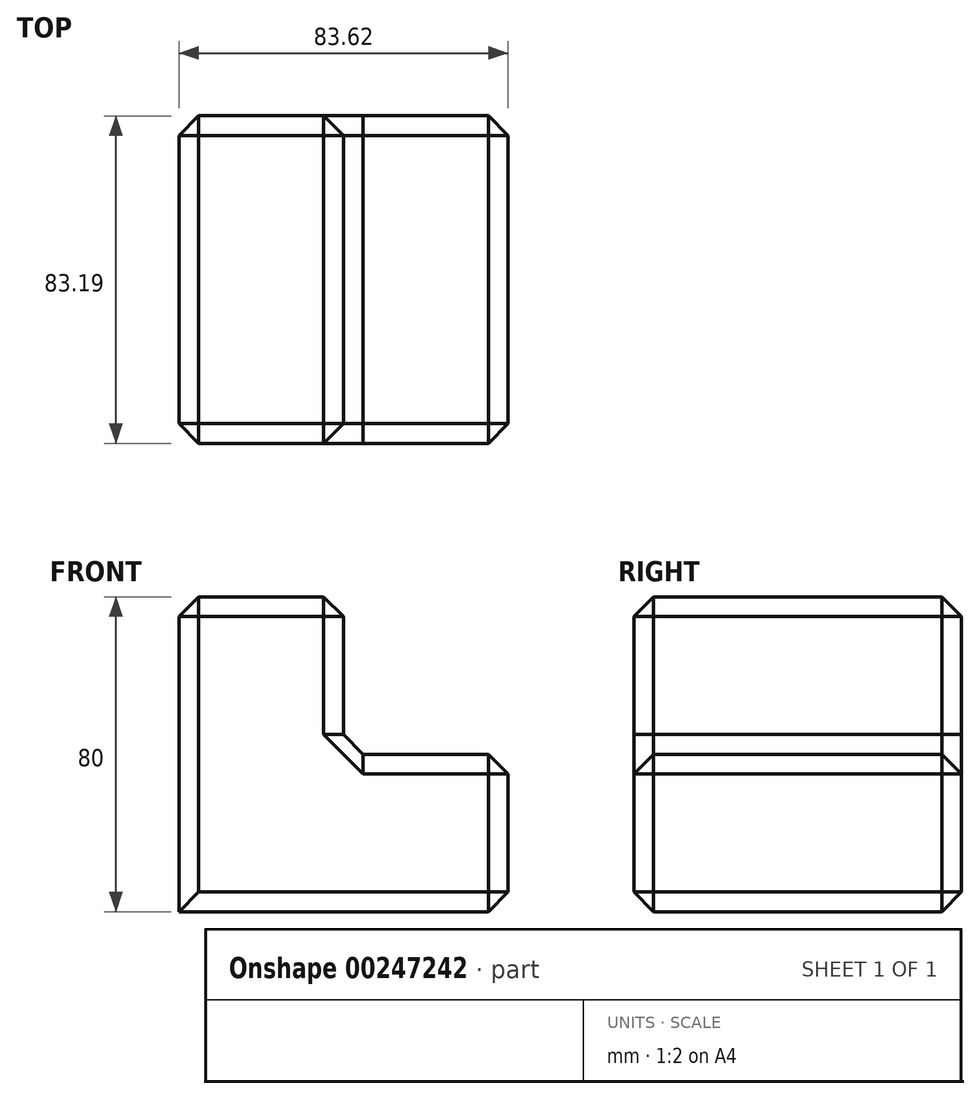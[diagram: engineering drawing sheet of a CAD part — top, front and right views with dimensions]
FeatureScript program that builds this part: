
annotation { "Feature Type Name" : "Feature", "Feature Type Description" : "" }
export const myFeature = defineFeature(function(context is Context, id is Id, definition is map)
    precondition{}
    {
        {
            var Q0;
            Q0=qCreatedBy(makeId("Top.planeOp"),FACE);
            var sketch = newSketch(context, id + "F0", { "sketchPlane" : qUnion([Q0])});
            skLineSegment(sketch, "E0.bottom", {"start": v(-59.13, -45.93) * mm, "end": v(24.5, -45.93) * mm});
            skLineSegment(sketch, "E0.top", {"start": v(-59.13, 37.26) * mm, "end": v(24.5, 37.26) * mm});
            skLineSegment(sketch, "E0.left", {"start": v(-59.13, -45.93) * mm, "end": v(-59.13, 37.26) * mm});
            skLineSegment(sketch, "E0.right", {"start": v(24.5, -45.93) * mm, "end": v(24.5, 37.26) * mm});
            skSolve(sketch);
        }
        {
            var Q0;
            Q0=makeQuery(id+"F0.imprint","IMPRINT",FACE,{"disambiguationData":[TD([[makeQuery(id+"F0.imprint","IMPRINT",EDGE,{"derivedFrom":sQuery(id+"F0.wireOp",EDGE,"E0.bottom")}),1.0]])]});
            extrude(context, id + "F1", {"entities" : qUnion([Q0]), "depth" : 40 * mm});
        }
        {
            var Q0;
            Q0=makeQuery(id+"F1.opExtrude","CAP_FACE",FACE,{"disambiguationData":[OSD([sQuery(id+"F0.wireOp",EDGE,"E0.bottom"),sQuery(id+"F0.wireOp",EDGE,"E0.top"),sQuery(id+"F0.wireOp",EDGE,"E0.left"),sQuery(id+"F0.wireOp",EDGE,"E0.right")])],"isStart":false});
            var sketch = newSketch(context, id + "F2", { "sketchPlane" : qUnion([Q0])});
            skLineSegment(sketch, "E1", {"start": v(-17.32, 37.26) * mm, "end": v(-17.32, -45.93) * mm});
            skSolve(sketch);
        }
        {
            var Q0;
            {var subQ1=sQuery(id+"F2.wireOp",EDGE,"E1");Q0=makeQuery(id+"F2.imprint","IMPRINT",FACE,{"disambiguationData":[TD([[makeQuery(id+"F2.imprint","IMPRINT",EDGE,{"derivedFrom":subQ1}),-1.0]])]});}
            extrude(context, id + "F3", {"entities" : qUnion([Q0]), "operationType" : NewBodyOperationType.ADD, "depth" : 40 * mm});
        }
        {
            var Q0;
            Q0=makeQuery(id+"F3.opExtrude","CAP_FACE",FACE,{"disambiguationData":[OSD([sQuery(id+"F0.wireOp",EDGE,"E0.bottom"),sQuery(id+"F0.wireOp",EDGE,"E0.top"),sQuery(id+"F0.wireOp",EDGE,"E0.left"),sQuery(id+"F2.wireOp",EDGE,"E1")])],"isStart":false});
            var Q1;
            {var subQ0=sQuery(id+"F0.wireOp",EDGE,"E0.bottom");Q1=makeQuery(id+"F3.boolean.opBoolean","MERGE",FACE,{"derivedFrom":[makeQuery(id+"F1.opExtrude","SWEPT_FACE",FACE,{"disambiguationData":[OSD([subQ0])]}),makeQuery(id+"F3.opExtrude","SWEPT_FACE",FACE,{"disambiguationData":[OSD([subQ0])]})]});}
            var Q2;
            Q2=makeQuery(id+"F1.opExtrude","CAP_FACE",FACE,{"disambiguationData":[OSD([sQuery(id+"F0.wireOp",EDGE,"E0.bottom"),sQuery(id+"F0.wireOp",EDGE,"E0.top"),sQuery(id+"F0.wireOp",EDGE,"E0.left"),sQuery(id+"F0.wireOp",EDGE,"E0.right")])],"isStart":false});
            var Q3;
            Q3=makeQuery(id+"F3.opExtrude","SWEPT_FACE",FACE,{"disambiguationData":[OSD([sQuery(id+"F2.wireOp",EDGE,"E1")])]});
            var Q4;
            Q4=makeQuery(id+"F1.opExtrude","SWEPT_FACE",FACE,{"disambiguationData":[OSD([sQuery(id+"F0.wireOp",EDGE,"E0.right")])]});
            var Q5;
            {var subQ0=sQuery(id+"F0.wireOp",EDGE,"E0.top");Q5=makeQuery(id+"F3.boolean.opBoolean","MERGE",FACE,{"derivedFrom":[makeQuery(id+"F1.opExtrude","SWEPT_FACE",FACE,{"disambiguationData":[OSD([subQ0])]}),makeQuery(id+"F3.opExtrude","SWEPT_FACE",FACE,{"disambiguationData":[OSD([subQ0])]})]});}
            chamfer(context, id + "F4", {"entities" : qUnion([Q0, Q1, Q2, Q3, Q4, Q5]), "width" : 5 * mm, "tangentPropagation" : true});
        }
    });
